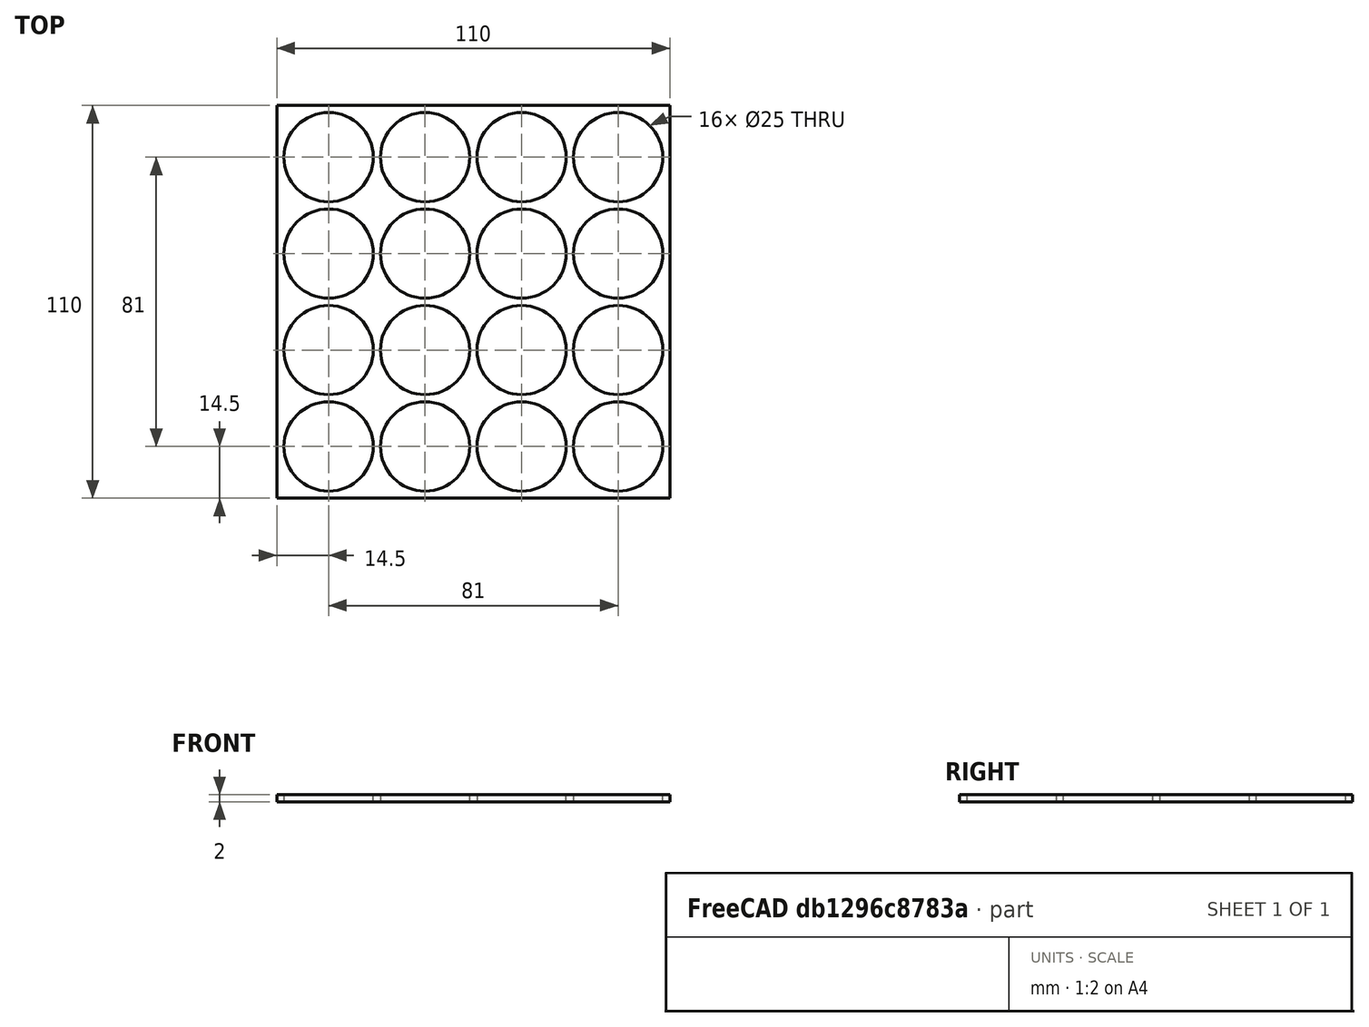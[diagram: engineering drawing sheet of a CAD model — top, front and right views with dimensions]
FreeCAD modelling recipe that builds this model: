
FCSTD DOCUMENT  (FreeCAD 0.20R29603 (Git))
Label: PillsHolder
License: All rights reserved
LicenseURL: http://en.wikipedia.org/wiki/All_rights_reserved
objects: Sketcher::SketchObject×1, PartDesign::Pad×1, PartDesign::Body×1
note: 4 computed .brp shape members not serialized (recipe doc carries the construction recipe); baked Part::Feature solids carry a one-line shape summary decoded from their .brp

FEATURE [Sketcher::SketchObject] Sketch
  FullyConstrained = true
  MapMode = 5
  Support = -> [XY_Plane]
  sketch-geometry (36):
    g0: LineSegment StartX=-55 StartY=55 StartZ=0 EndX=-55 EndY=-55 EndZ=0
    g1: LineSegment StartX=-55 StartY=-55 StartZ=0 EndX=55 EndY=-55 EndZ=0
    g2: LineSegment StartX=55 StartY=-55 StartZ=0 EndX=55 EndY=55 EndZ=0
    g3: LineSegment StartX=55 StartY=55 StartZ=0 EndX=-55 EndY=55 EndZ=0
    g4: GeomPoint X=0 Y=0 Z=0
    g5: Circle CenterX=-40.5 CenterY=40.5 CenterZ=0 NormalX=0 NormalY=0 NormalZ=1 AngleXU=0 Radius=12.5
    g6: Circle CenterX=-13.5 CenterY=40.5 CenterZ=0 NormalX=0 NormalY=0 NormalZ=1 AngleXU=0 Radius=12.5
    g7: LineSegment StartX=-40.5 StartY=40.5 StartZ=0 EndX=-13.5 EndY=40.5 EndZ=0
    g8: Circle CenterX=13.5 CenterY=40.5 CenterZ=0 NormalX=0 NormalY=0 NormalZ=1 AngleXU=0 Radius=12.5
    g9: LineSegment StartX=-13.5 StartY=40.5 StartZ=0 EndX=13.5 EndY=40.5 EndZ=0
    g10: Circle CenterX=40.5 CenterY=40.5 CenterZ=0 NormalX=0 NormalY=0 NormalZ=1 AngleXU=0 Radius=12.5
    g11: LineSegment StartX=13.5 StartY=40.5 StartZ=0 EndX=40.5 EndY=40.5 EndZ=0
    g12: Circle CenterX=-40.5 CenterY=13.5 CenterZ=0 NormalX=0 NormalY=0 NormalZ=1 AngleXU=0 Radius=12.5
    g13: LineSegment StartX=-40.5 StartY=40.5 StartZ=0 EndX=-40.5 EndY=13.5 EndZ=0
    g14: Circle CenterX=-13.5 CenterY=13.5 CenterZ=0 NormalX=0 NormalY=0 NormalZ=1 AngleXU=0 Radius=12.5
    g15: LineSegment StartX=-40.5 StartY=13.5 StartZ=0 EndX=-13.5 EndY=13.5 EndZ=0
    g16: Circle CenterX=13.5 CenterY=13.5 CenterZ=0 NormalX=0 NormalY=0 NormalZ=1 AngleXU=0 Radius=12.5
    g17: LineSegment StartX=-13.5 StartY=13.5 StartZ=0 EndX=13.5 EndY=13.5 EndZ=0
    g18: Circle CenterX=40.5 CenterY=13.5 CenterZ=0 NormalX=0 NormalY=0 NormalZ=1 AngleXU=0 Radius=12.5
    g19: LineSegment StartX=13.5 StartY=13.5 StartZ=0 EndX=40.5 EndY=13.5 EndZ=0
    g20: Circle CenterX=-40.5 CenterY=-13.5 CenterZ=0 NormalX=0 NormalY=0 NormalZ=1 AngleXU=0 Radius=12.5
    g21: LineSegment StartX=-40.5 StartY=13.5 StartZ=0 EndX=-40.5 EndY=-13.5 EndZ=0
    g22: Circle CenterX=-13.5 CenterY=-13.5 CenterZ=0 NormalX=0 NormalY=0 NormalZ=1 AngleXU=0 Radius=12.5
    g23: LineSegment StartX=-40.5 StartY=-13.5 StartZ=0 EndX=-13.5 EndY=-13.5 EndZ=0
    g24: Circle CenterX=13.5 CenterY=-13.5 CenterZ=0 NormalX=0 NormalY=0 NormalZ=1 AngleXU=0 Radius=12.5
    g25: LineSegment StartX=-13.5 StartY=-13.5 StartZ=0 EndX=13.5 EndY=-13.5 EndZ=0
    g26: Circle CenterX=40.5 CenterY=-13.5 CenterZ=0 NormalX=0 NormalY=0 NormalZ=1 AngleXU=0 Radius=12.5
    g27: LineSegment StartX=13.5 StartY=-13.5 StartZ=0 EndX=40.5 EndY=-13.5 EndZ=0
    g28: Circle CenterX=-40.5 CenterY=-40.5 CenterZ=0 NormalX=0 NormalY=0 NormalZ=1 AngleXU=0 Radius=12.5
    g29: LineSegment StartX=-40.5 StartY=-13.5 StartZ=0 EndX=-40.5 EndY=-40.5 EndZ=0
    g30: Circle CenterX=-13.5 CenterY=-40.5 CenterZ=0 NormalX=0 NormalY=0 NormalZ=1 AngleXU=0 Radius=12.5
    g31: LineSegment StartX=-40.5 StartY=-40.5 StartZ=0 EndX=-13.5 EndY=-40.5 EndZ=0
    g32: Circle CenterX=13.5 CenterY=-40.5 CenterZ=0 NormalX=0 NormalY=0 NormalZ=1 AngleXU=0 Radius=12.5
    g33: LineSegment StartX=-13.5 StartY=-40.5 StartZ=0 EndX=13.5 EndY=-40.5 EndZ=0
    g34: Circle CenterX=40.5 CenterY=-40.5 CenterZ=0 NormalX=0 NormalY=0 NormalZ=1 AngleXU=0 Radius=12.5
    g35: LineSegment StartX=13.5 StartY=-40.5 StartZ=0 EndX=40.5 EndY=-40.5 EndZ=0
  constraints (90):
    c: Coincident(g0,g1)
    c: Coincident(g1,g2)
    c: Coincident(g2,g3)
    c: Coincident(g3,g0)
    c: Horizontal(g1)
    c: Horizontal(g3)
    c: Vertical(g0)
    c: Vertical(g2)
    c: Symmetric(g1,g0,g4)
    c: Coincident(g4,g-1)
    c: DistanceX(g3,g3) = 110
    c: DistanceY(g0,g0) = 110
    c: Diameter(g5) = 25
    c: DistanceX(g0,g5) = 14.5
    c: DistanceY(g5,g0) = 14.5
    c: Diameter(g6) = 25
    c: Coincident(g5,g7)
    c: Coincident(g6,g7)
    c: Distance(g7) = 27
    c: Angle(g7) = 0
    c: Diameter(g8) = 25
    c: Coincident(g6,g9)
    c: Coincident(g8,g9)
    c: Equal(g7,g9)
    c: Parallel(g9,g7)
    c: Diameter(g10) = 25
    c: Coincident(g8,g11)
    c: Coincident(g10,g11)
    c: Equal(g7,g11)
    c: Parallel(g11,g7)
    c: Diameter(g12) = 25
    c: Coincident(g5,g13)
    c: Coincident(g12,g13)
    c: Equal(g13,g7)
    c: Perpendicular(g13,g7)
    c: Diameter(g14) = 25
    c: Coincident(g12,g15)
    c: Coincident(g14,g15)
    c: Equal(g7,g15)
    c: Parallel(g15,g7)
    c: Diameter(g16) = 25
    c: Coincident(g14,g17)
    c: Coincident(g16,g17)
    c: Equal(g7,g17)
    c: Parallel(g17,g7)
    c: Diameter(g18) = 25
    c: Coincident(g16,g19)
    c: Coincident(g18,g19)
    c: Equal(g7,g19)
    c: Parallel(g19,g7)
    c: Diameter(g20) = 25
    c: Coincident(g12,g21)
    c: Coincident(g20,g21)
    c: Equal(g13,g21)
    c: Perpendicular(g21,g7)
    c: Diameter(g22) = 25
    c: Coincident(g20,g23)
    c: Coincident(g22,g23)
    c: Equal(g7,g23)
    c: Parallel(g23,g7)
    c: Diameter(g24) = 25
    c: Coincident(g22,g25)
    c: Coincident(g24,g25)
    c: Equal(g7,g25)
    c: Parallel(g25,g7)
    c: Diameter(g26) = 25
    c: Coincident(g24,g27)
    c: Coincident(g26,g27)
    c: Equal(g7,g27)
    c: Parallel(g27,g7)
    c: Diameter(g28) = 25
    c: Coincident(g20,g29)
    c: Coincident(g28,g29)
    c: Equal(g13,g29)
    c: Perpendicular(g29,g7)
    c: Diameter(g30) = 25
    c: Coincident(g28,g31)
    c: Coincident(g30,g31)
    c: Equal(g7,g31)
    c: Parallel(g31,g7)
    c: Diameter(g32) = 25
    c: Coincident(g30,g33)
    c: Coincident(g32,g33)
    c: Equal(g7,g33)
    c: Parallel(g33,g7)
    c: Diameter(g34) = 25
    c: Coincident(g32,g35)
    c: Coincident(g34,g35)
    c: Equal(g7,g35)
    c: Parallel(g35,g7)
FEATURE [PartDesign::Pad] Pad
  Direction = (0,0,1)
  Length = 2
  Length2 = 10
  Profile = -> Sketch
  ReferenceAxis = -> Sketch [N_Axis]
  Type = 0
FEATURE [PartDesign::Body] Body
  Group = -> [Sketch,Pad]
  Origin = -> Origin
  Tip = -> Pad
